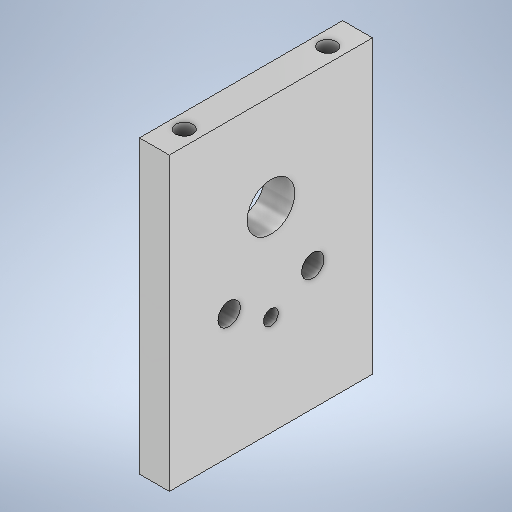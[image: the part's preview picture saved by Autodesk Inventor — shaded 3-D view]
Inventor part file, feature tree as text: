
AUTODESK INVENTOR PART (.ipt)
format: ipt  version: 2025.1 (Build 291241020, 241B)  size: 293,888 bytes
history: native  units: in
note: dims shown in document units (in); Inventor stores cm internally (conversion verified against a paired STEP export)
features: sketch x8, extrude x7, hole x1, projected_geometry x1
ambient origin geometry x8: Origin, YZ Plane, XZ Plane, XY Plane, X Axis, Y Axis, Z Axis, Center Point
bodies: Solid1 (feature_tree)
feature tree (17):
  extrude  "Extrusion1"  Depth=2.5in
  extrude  "Extrusion2"  Depth=0.0625in
  extrude  "Extrusion3"  Depth=0.0625in
  extrude  "Extrusion4"  Depth=0.3976in
  extrude  "Extrusion5"  TaperAngle=0.0deg  [1 undecoded]
  extrude  "Extrusion6"  Depth=0.8in
  extrude  "Extrusion7"  Depth=0.6in
  hole  "Hole1"  [1 undecoded]
  sketch  "Sketch1"  dims[d0=11.0in d1=2.5in]
  sketch  "Sketch2"  dims[d2=1.7in d3=0.0in d4=0.0625in]
  sketch  "Sketch3"  dims[d5=0.0625in d6=0.0625in]
  sketch  "Sketch4"  dims[d7=1.5in d8=0.0in d9=0.3976in]
  sketch  "Sketch5"  dims[d10=0.8in d11=0.0in d12=0.0in]
  sketch  "Sketch6"  dims[d13=0.125in d15=0.8in]
  sketch  "Sketch7"  dims[d16=0.5in d17=0.6in]
  projected_geometry  "Projected Loop1"
  sketch  "Sketch8"  dims[d18=0.1875in d19=1.0in d20=0.0in d21=0.125in d22=0.6102in d23=0.6102in d24=1.0in d25=0.0in d26=0.0in d27=0.0in d28=0.25in d29=0.0in d30=0.25in d31=0.25in d32=0.144in d33=0.75in d34=0.563in d35=0.12in d36=0.5635in d37=0.885in d38=0.8108in]
note: 2 required parameter values undecoded (feature->parameter linkage not recoverable at this tier; creation-order binding heuristic only, values carry confidence <= 0.55)
